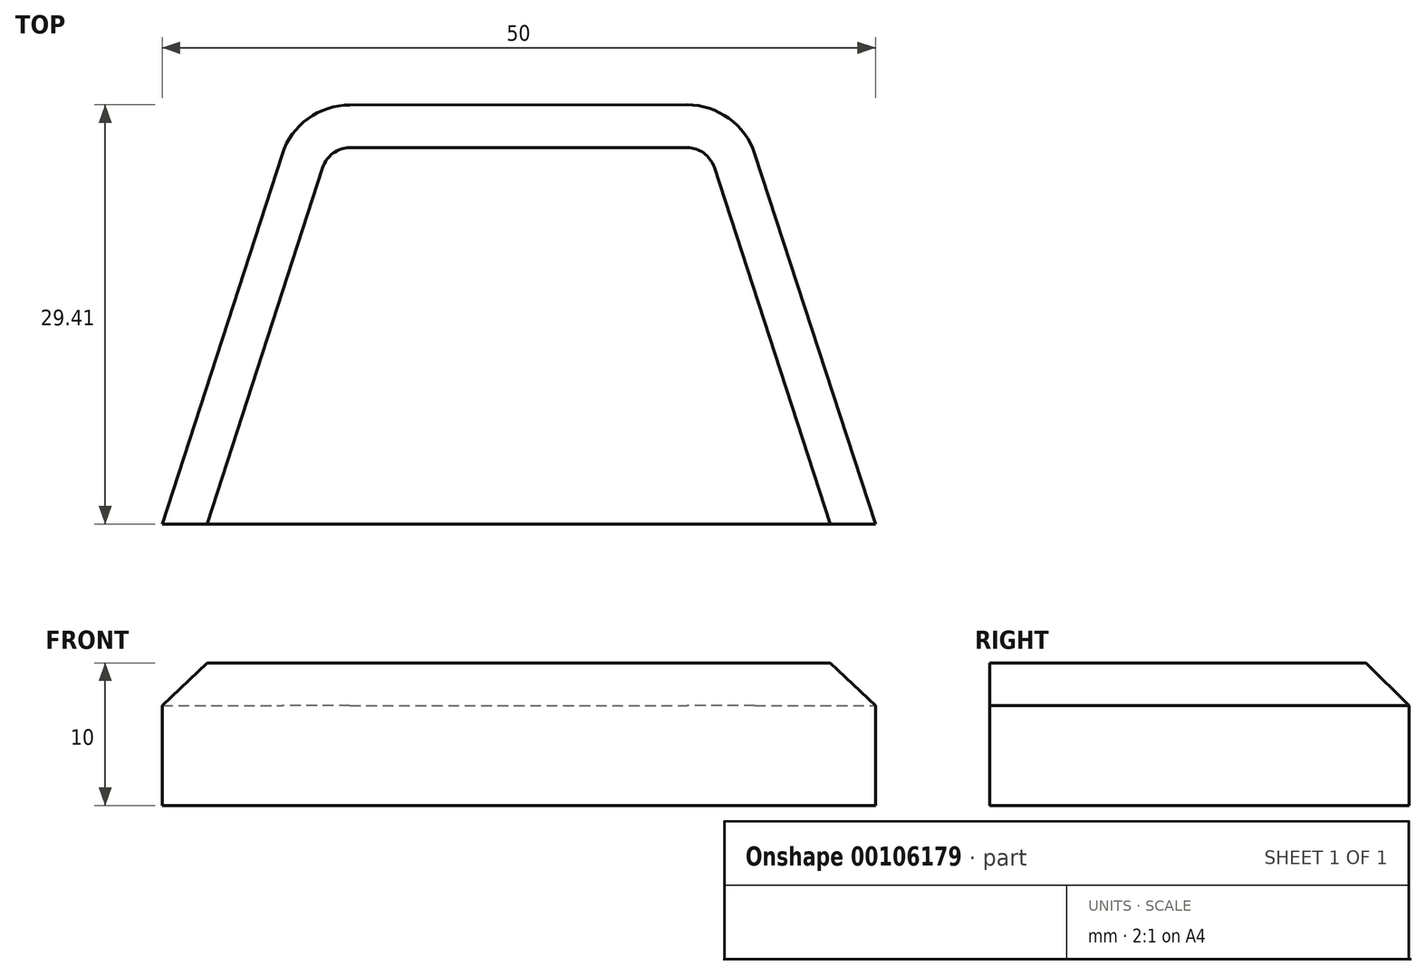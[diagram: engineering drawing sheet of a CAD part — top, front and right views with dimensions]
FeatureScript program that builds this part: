
annotation { "Feature Type Name" : "Feature", "Feature Type Description" : "" }
export const myFeature = defineFeature(function(context is Context, id is Id, definition is map)
    precondition{}
    {
        {
            var Q0;
            Q0=qCreatedBy(makeId("Top.planeOp"),FACE);
            var sketch = newSketch(context, id + "F0", { "sketchPlane" : qUnion([Q0])});
            skArc(sketch, "E0.cCircle", {"start": v(19.64, -8.14) * mm, "mid": v(0, 21.26) * mm, "end": v(-19.64, -8.14) * mm, "construction": true});
            skLineSegment(sketch, "E0.2", {"start": v(-25, -8.14) * mm, "end": v(-15.46, 21.25) * mm});
            skLineSegment(sketch, "E0.3", {"start": v(-15.46, 21.25) * mm, "end": v(15.43, 21.27) * mm});
            skLineSegment(sketch, "E0.4", {"start": v(15.43, 21.27) * mm, "end": v(25, -8.14) * mm});
            skPoint(sketch, "E0.0.midPoint", {"position": v(10.09, -18.72) * mm});
            skLineSegment(sketch, "E1", {"start": v(25, -8.14) * mm, "end": v(-25, -8.14) * mm});
            skPoint(sketch, "E2.orphan", {"position": v(-4.84, -29.3) * mm});
            skSolve(sketch);
        }
        {
            var Q0;
            Q0 = qSketchRegion(id + "F0", true);
            extrude(context, id + "F1", {"entities" : qUnion([Q0]), "depth" : 10 * mm});
        }
        {
            var Q0;
            Q0=makeQuery(id+"F1.opExtrude","SWEPT_EDGE",EDGE,{"disambiguationData":[OSD([sQuery(id+"F0.wireOp",EDGE,"E0.2"),sQuery(id+"F0.wireOp",EDGE,"E0.3")])]});
            var Q1;
            Q1=makeQuery(id+"F1.opExtrude","SWEPT_EDGE",EDGE,{"disambiguationData":[OSD([sQuery(id+"F0.wireOp",EDGE,"E0.3"),sQuery(id+"F0.wireOp",EDGE,"E0.4")])]});
            fillet(context, id + "F2", {"entities" : qUnion([Q0, Q1]), "radius" : 5 * mm, "tangentPropagation" : true, "allowEdgeOverflow" : false});
        }
        {
            var Q0;
            Q0=makeQuery(id+"F1.opExtrude","CAP_EDGE",EDGE,{"disambiguationData":[OSD([sQuery(id+"F0.wireOp",EDGE,"E0.3")])],"isStart":false});
            var Q1;
            Q1=makeQuery(id+"F1.opExtrude","CAP_EDGE",EDGE,{"disambiguationData":[OSD([sQuery(id+"F0.wireOp",EDGE,"E0.4")])],"isStart":false});
            var Q2;
            {var subQ0=sQuery(id+"F0.wireOp",EDGE,"E0.4");var subQ1=sQuery(id+"F0.wireOp",EDGE,"E0.3");Q2=makeQuery(id+"F2.opFillet","BLEND_EDGE",EDGE,{"blendedFrom":[makeQuery(id+"F1.opExtrude","SWEPT_EDGE",EDGE,{"disambiguationData":[OSD([subQ1,subQ0])]}),makeQuery(id+"F1.opExtrude","CAP_FACE",FACE,{"disambiguationData":[OSD([sQuery(id+"F0.wireOp",EDGE,"E0.2"),subQ1,subQ0,sQuery(id+"F0.wireOp",EDGE,"E1")])],"isStart":false})],"blendedInto":[makeQuery(id+"F1.opExtrude","CAP_FACE",FACE,{"disambiguationData":[OSD([sQuery(id+"F0.wireOp",EDGE,"E0.2"),subQ1,subQ0,sQuery(id+"F0.wireOp",EDGE,"E1")])],"isStart":false})]});}
            var Q3;
            Q3=makeQuery(id+"F1.opExtrude","CAP_EDGE",EDGE,{"disambiguationData":[OSD([sQuery(id+"F0.wireOp",EDGE,"E0.2")])],"isStart":false});
            var Q4;
            {var subQ0=sQuery(id+"F0.wireOp",EDGE,"E0.3");var subQ1=sQuery(id+"F0.wireOp",EDGE,"E0.2");Q4=makeQuery(id+"F2.opFillet","BLEND_EDGE",EDGE,{"blendedFrom":[makeQuery(id+"F1.opExtrude","SWEPT_EDGE",EDGE,{"disambiguationData":[OSD([subQ1,subQ0])]}),makeQuery(id+"F1.opExtrude","CAP_FACE",FACE,{"disambiguationData":[OSD([subQ1,subQ0,sQuery(id+"F0.wireOp",EDGE,"E0.4"),sQuery(id+"F0.wireOp",EDGE,"E1")])],"isStart":false})],"blendedInto":[makeQuery(id+"F1.opExtrude","CAP_FACE",FACE,{"disambiguationData":[OSD([subQ1,subQ0,sQuery(id+"F0.wireOp",EDGE,"E0.4"),sQuery(id+"F0.wireOp",EDGE,"E1")])],"isStart":false})]});}
            chamfer(context, id + "F3", {"entities" : qUnion([Q0, Q1, Q2, Q3, Q4]), "width" : 3 * mm, "tangentPropagation" : true});
        }
    });
